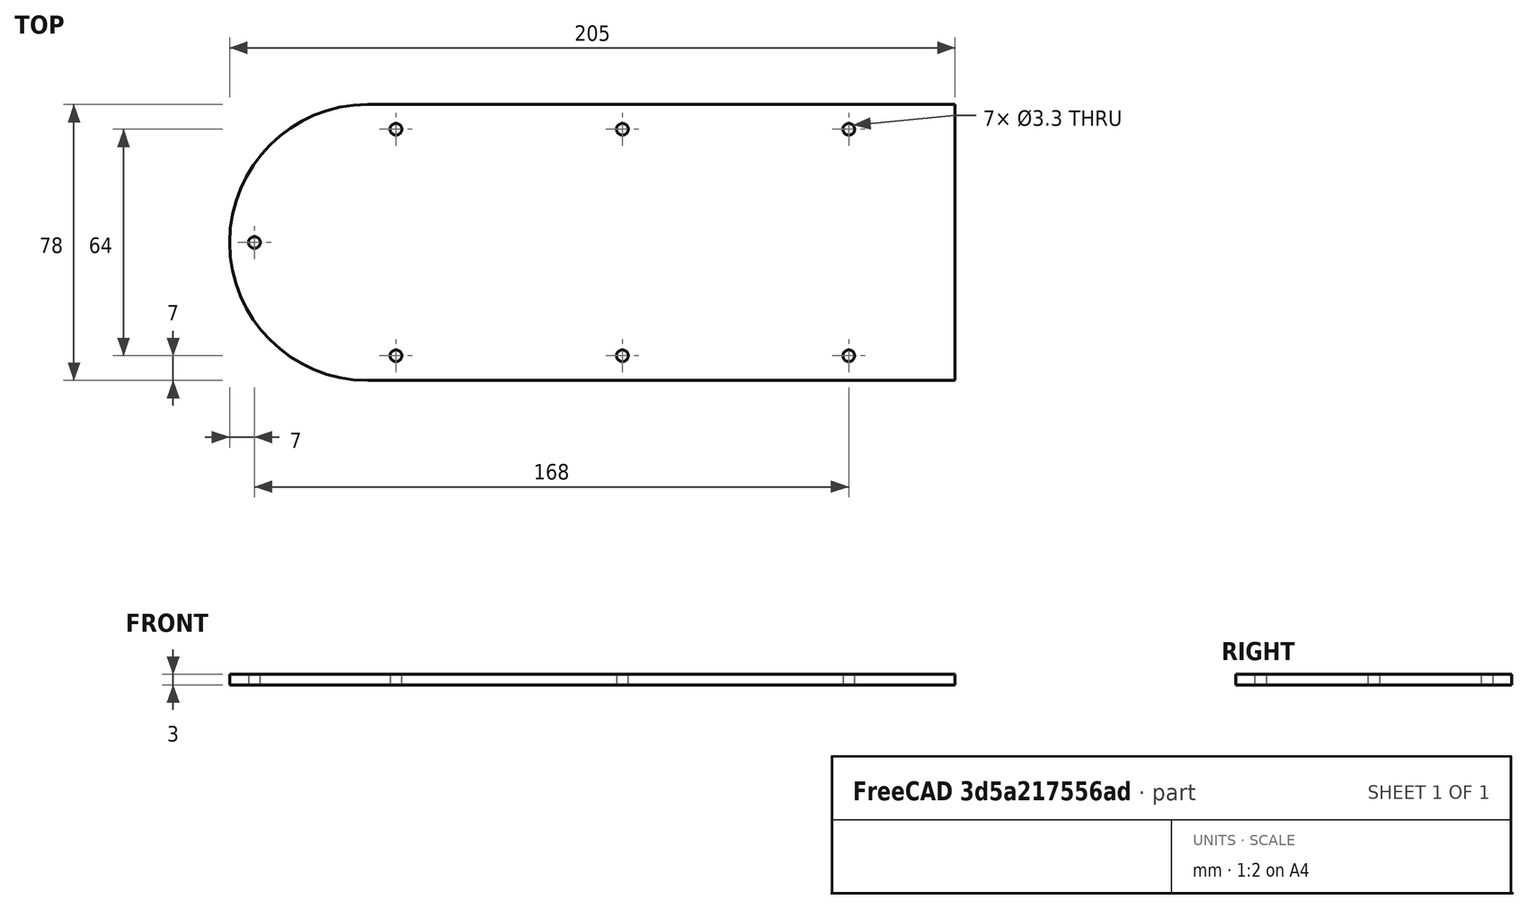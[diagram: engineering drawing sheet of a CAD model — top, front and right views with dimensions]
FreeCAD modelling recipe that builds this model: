
FCSTD DOCUMENT  (FreeCAD 0.19R)
Label: Arm1_cover_modified
License: All rights reserved
LicenseURL: http://en.wikipedia.org/wiki/All_rights_reserved
objects: Sketcher::SketchObject×1, PartDesign::Pad×1, PartDesign::Body×1, Part::Part2DObjectPython×1
note: 5 computed .brp shape members not serialized (recipe doc carries the construction recipe); baked Part::Feature solids carry a one-line shape summary decoded from their .brp

FEATURE [Sketcher::SketchObject] Sketch
  FullyConstrained = true
  MapMode = 5
  Support = -> [XY_Plane]
  sketch-geometry (15):
    g0: ArcOfCircle CenterX=0 CenterY=0 CenterZ=0 NormalX=0 NormalY=0 NormalZ=1 AngleXU=0 Radius=39 StartAngle=1.5708 EndAngle=4.71239
    g1: LineSegment StartX=2.4e-15 StartY=39 StartZ=0 EndX=166 EndY=39 EndZ=0
    g2: LineSegment StartX=166 StartY=39 StartZ=0 EndX=166 EndY=-39 EndZ=0
    g3: LineSegment StartX=166 StartY=-39 StartZ=0 EndX=0 EndY=-39 EndZ=0
    g4: LineSegment StartX=8 StartY=32 StartZ=0 EndX=136 EndY=32 EndZ=0
    g5: LineSegment StartX=136 StartY=32 StartZ=0 EndX=136 EndY=-32 EndZ=0
    g6: LineSegment StartX=136 StartY=-32 StartZ=0 EndX=8 EndY=-32 EndZ=0
    g7: LineSegment StartX=8 StartY=-32 StartZ=0 EndX=8 EndY=32 EndZ=0
    g8: Circle CenterX=-32 CenterY=0 CenterZ=0 NormalX=0 NormalY=0 NormalZ=1 AngleXU=0 Radius=1.65
    g9: Circle CenterX=8 CenterY=32 CenterZ=0 NormalX=0 NormalY=0 NormalZ=1 AngleXU=0 Radius=1.65
    g10: Circle CenterX=72 CenterY=32 CenterZ=0 NormalX=0 NormalY=0 NormalZ=1 AngleXU=0 Radius=1.65
    g11: Circle CenterX=136 CenterY=32 CenterZ=0 NormalX=0 NormalY=0 NormalZ=1 AngleXU=0 Radius=1.65
    g12: Circle CenterX=8 CenterY=-32 CenterZ=0 NormalX=0 NormalY=0 NormalZ=1 AngleXU=0 Radius=1.65
    g13: Circle CenterX=72 CenterY=-32 CenterZ=0 NormalX=0 NormalY=0 NormalZ=1 AngleXU=0 Radius=1.65
    g14: Circle CenterX=136 CenterY=-32 CenterZ=0 NormalX=0 NormalY=0 NormalZ=1 AngleXU=0 Radius=1.65
  constraints (39):
    c: Coincident(g0,g-1)
    c: PointOnObject(g0,g-2)
    c: PointOnObject(g0,g-2)
    c: DistanceY(g0,g0) = 39
    c: Coincident(g1,g2)
    c: Coincident(g2,g3)
    c: Horizontal(g1)
    c: Horizontal(g3)
    c: Vertical(g2)
    c: Coincident(g1,g0)
    c: Coincident(g3,g0)
    c: DistanceX(g1,g1) = 166
    c: Coincident(g4,g5)
    c: Coincident(g5,g6)
    c: Coincident(g6,g7)
    c: Coincident(g7,g4)
    c: Horizontal(g4)
    c: Horizontal(g6)
    c: Vertical(g5)
    c: PointOnObject(g8,g-1)
    c: Coincident(g9,g4)
    c: Coincident(g11,g4)
    c: Coincident(g12,g6)
    c: PointOnObject(g13,g6)
    c: Coincident(g14,g5)
    c: Equal(g14,g11)
    c: Equal(g11,g10)
    c: Equal(g10,g13)
    c: Equal(g13,g12)
    c: Equal(g12,g9)
    c: Equal(g9,g8)
    c: Radius(g8) = 1.65
    c: DistanceY(g12,g9) = 64
    c: DistanceX(g8) = -32
    c: Symmetric(g9,g11,g10)
    c: Vertical(g10,g13)
    c: Symmetric(g12,g9,g-1)
    c: DistanceX(g9,g11) = 128
    c: DistanceX(g12) = 8
FEATURE [PartDesign::Pad] Pad
  Direction = (1,1,1)
  Length = 3
  Length2 = 100
  Profile = -> Sketch
  Type = 0
FEATURE [PartDesign::Body] Body
  Group = -> [Sketch,Pad]
  Origin = -> Origin
  Tip = -> Pad
FEATURE [Part::Part2DObjectPython] Shape2DView  # Draft 2D object (typed FeaturePython)
  Base = -> Pad
  FuseArch = false
  HiddenLines = false
  InPlace = true
  Projection = (0,0,1)
  ProjectionMode = 0
  SegmentLength = 0.05
  Tessellation = false
  VisibleOnly = false
